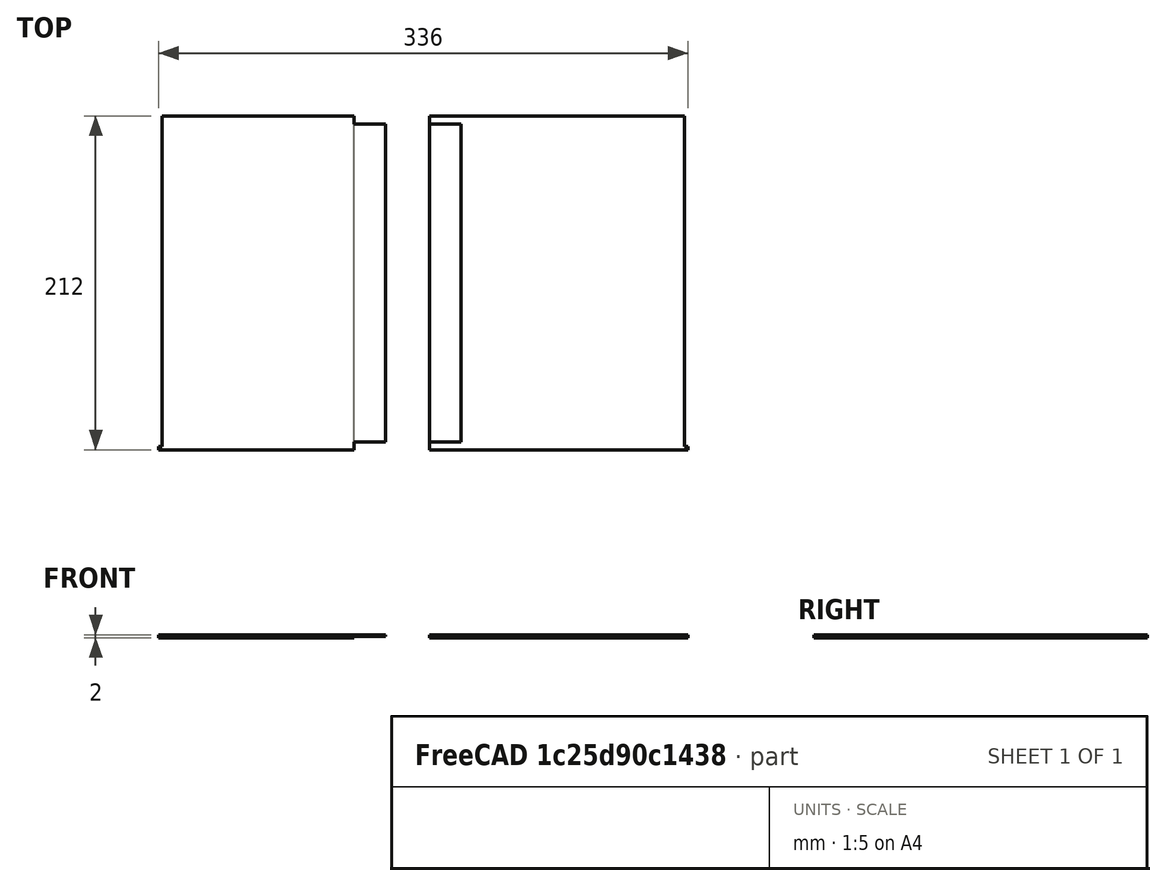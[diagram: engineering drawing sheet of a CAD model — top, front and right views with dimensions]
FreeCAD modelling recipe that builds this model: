
FCSTD DOCUMENT  (FreeCAD 0.17R13522 (Git))
Label: tapa
License: CreativeCommons Attribution-ShareAlike
LicenseURL: http://creativecommons.org/licenses/by-sa/4.0/
objects: Part::Box×9, Part::Fuse×6, Part::Cut×5, Part::Feature×4
note: 24 computed .brp shape members not serialized (recipe doc carries the construction recipe); baked Part::Feature solids carry a one-line shape summary decoded from their .brp

FEATURE [Part::Box] Box  label="tapa"
  AttacherType = Attacher::AttachEngine3D
  Height = 2
  Length = 284
  Width = 212
FEATURE [Part::Box] Box001  label="Cube"
  AttacherType = Attacher::AttachEngine3D
  Height = 2
  Length = 2
  Placement = pos=(-2,0,0) rot=(0,0,1;0rad)
  Width = 2
FEATURE [Part::Fuse] Fusion
  Base = -> Box
  Refine = true
  Tool = -> Box001
FEATURE [Part::Box] Box002  label="Cube001"
  AttacherType = Attacher::AttachEngine3D
  Height = 2
  Length = 2
  Placement = pos=(284,0,0) rot=(0,0,1;0rad)
  Width = 2
FEATURE [Part::Fuse] Fusion001  label="tapa_entera"
  Base = -> Fusion
  Refine = true
  Tool = -> Box002
FEATURE [Part::Feature] Fusion001001  label="tapa_entera001"
  Placement = pos=(0,250,0) rot=(0,0,1;0rad)
  shape: bbox 288 x 212 x 2 mm, 10 faces (baked)
FEATURE [Part::Box] Box003  label="Cube002"
  AttacherType = Attacher::AttachEngine3D
  Height = 1
  Length = 164
  Placement = pos=(-2,0,9) rot=(0,0,1;0rad)
  Width = 212
FEATURE [Part::Box] Box004  label="Cube003"
  AttacherType = Attacher::AttachEngine3D
  Height = 1
  Length = 164
  Placement = pos=(122,250,2) rot=(0,0,1;0rad)
  Width = 212
FEATURE [Part::Box] Box005  label="Cube004"
  AttacherType = Attacher::AttachEngine3D
  Height = 7
  Length = 144
  Placement = pos=(-2,0,3) rot=(0,0,1;0rad)
  Width = 212
FEATURE [Part::Box] Box006  label="Cube005"
  AttacherType = Attacher::AttachEngine3D
  Height = 10
  Length = 142
  Placement = pos=(144,250,3) rot=(0,0,1;0rad)
  Width = 212
FEATURE [Part::Fuse] Fusion001003
  Base = -> Box004
  Placement = pos=(0,0,-2) rot=(0,0,1;0rad)
  Refine = true
  Tool = -> Box006
FEATURE [Part::Cut] Cut  label="tapa_izquierda_2"
  Base = -> Fusion001001
  Placement = pos=(0,-250,0) rot=(0,0,1;0rad)
  Refine = true
  Tool = -> Fusion001003
FEATURE [Part::Fuse] Fusion001004
  Base = -> Box003
  Placement = pos=(-20,0,-8) rot=(0,0,1;0rad)
  Refine = true
  Tool = -> Box005
FEATURE [Part::Cut] Cut001  label="tapa_derecha"
  Base = -> Fusion001
  Placement = pos=(0,0,-50) rot=(0,0,1;0rad)
  Refine = true
  Tool = -> Fusion001004
FEATURE [Part::Box] Box007  label="Cube006"
  AttacherType = Attacher::AttachEngine3D
  Height = 10
  Length = 2
  Placement = pos=(142,-2,0) rot=(0,0,1;0rad)
  Width = 216
FEATURE [Part::Cut] Cut002  label="tapa_izquierda"
  Base = -> Cut
  Refine = true
  Tool = -> Box007
FEATURE [Part::Box] Box008  label="Cube007"
  AttacherType = Attacher::AttachEngine3D
  Height = 1
  Length = 20
  Placement = pos=(122,0,-49) rot=(0,0,1;0rad)
  Width = 5
FEATURE [Part::Feature] Box008001  label="Cube008"
  Placement = pos=(122,0,1) rot=(0,0,1;0rad)
  shape: bbox 20 x 5 x 1 mm, 6 faces (baked)
FEATURE [Part::Cut] Cut003
  Base = -> Cut002
  Refine = true
  Tool = -> Box008001
FEATURE [Part::Fuse] Fusion001005
  Base = -> Cut001
  Refine = true
  Tool = -> Box008
FEATURE [Part::Feature] Box008002  label="Cube009"
  Placement = pos=(122,207,-49) rot=(0,0,1;0rad)
  shape: bbox 20 x 5 x 1 mm, 6 faces (baked)
FEATURE [Part::Feature] Box008002001  label="Cube010"
  Placement = pos=(122,207,1) rot=(0,0,1;0rad)
  shape: bbox 20 x 5 x 1 mm, 6 faces (baked)
FEATURE [Part::Fuse] Fusion001006  label="tapa_drecha_con_encastres"
  Base = -> Fusion001005
  Placement = pos=(48,0,50) rot=(0,0,1;0rad)
  Refine = true
  Tool = -> Box008002
FEATURE [Part::Cut] Cut004  label="tapa_izquierda_con_encastres"
  Base = -> Cut003
  Refine = true
  Tool = -> Box008002001
